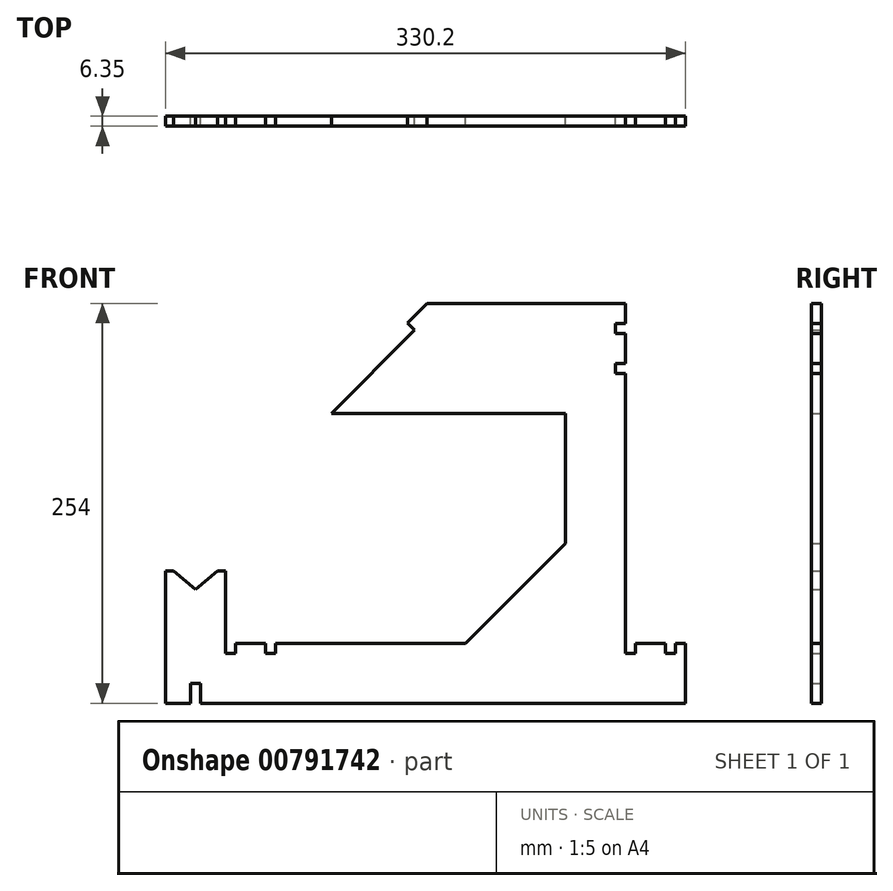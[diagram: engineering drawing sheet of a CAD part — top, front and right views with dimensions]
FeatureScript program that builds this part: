
annotation { "Feature Type Name" : "Feature", "Feature Type Description" : "" }
export const myFeature = defineFeature(function(context is Context, id is Id, definition is map)
    precondition{}
    {
        {
            var Q0;
            Q0=qCreatedBy(makeId("Front.planeOp"),FACE);
            var sketch = newSketch(context, id + "F0", { "sketchPlane" : qUnion([Q0])});
            skLineSegment(sketch, "E0", {"start": v(-82.64, -105.94) * mm, "end": v(-146.14, -169.44) * mm});
            skLineSegment(sketch, "E1", {"start": v(-146.14, -169.44) * mm, "end": v(-266.8, -169.44) * mm});
            skLineSegment(sketch, "E2", {"start": v(-336.64, -207.54) * mm, "end": v(-336.64, -123.4) * mm});
            skCircle(sketch, "E3", {"center": v(-317.6, -118.64) * mm, "radius": 12.7 * mm, "construction": true});
            skLineSegment(sketch, "E4.0", {"start": v(-336.64, -123.4) * mm, "end": v(-331.67, -123.4) * mm});
            skLineSegment(sketch, "E5", {"start": v(-298.54, -123.4) * mm, "end": v(-298.54, -175.79) * mm});
            skLineSegment(sketch, "E6.trimOffspring", {"start": v(-303.5, -123.4) * mm, "end": v(-298.54, -123.4) * mm});
            skPoint(sketch, "E7.orphan", {"position": v(-317.6, -130.6) * mm});
            skLineSegment(sketch, "E8.0", {"start": v(-331.67, -123.4) * mm, "end": v(-317.6, -135.21) * mm});
            skLineSegment(sketch, "E9.0", {"start": v(-303.5, -123.4) * mm, "end": v(-317.6, -135.21) * mm});
            skLineSegment(sketch, "E10", {"start": v(-325.75, -128.36) * mm, "end": v(-317.6, -118.64) * mm, "construction": true});
            skLineSegment(sketch, "E11", {"start": v(-309.43, -128.36) * mm, "end": v(-317.6, -118.64) * mm, "construction": true});
            skLineSegment(sketch, "E12.0", {"start": v(-6.44, -207.54) * mm, "end": v(-314.42, -207.54) * mm});
            skLineSegment(sketch, "E13", {"start": v(-44.54, 46.46) * mm, "end": v(-44.54, 33.76) * mm});
            skLineSegment(sketch, "E14", {"start": v(-38.2, -169.44) * mm, "end": v(-19.14, -169.44) * mm});
            skLineSegment(sketch, "E15", {"start": v(-6.44, -169.44) * mm, "end": v(-6.44, -207.54) * mm});
            skLineSegment(sketch, "E16", {"start": v(-82.64, -105.94) * mm, "end": v(-82.64, -23.39) * mm});
            skLineSegment(sketch, "E17", {"start": v(-231.32, -23.39) * mm, "end": v(-82.64, -23.39) * mm});
            skLineSegment(sketch, "E18.0", {"start": v(-170.45, 46.46) * mm, "end": v(-44.54, 46.46) * mm});
            skLineSegment(sketch, "E19.top", {"start": v(-320.77, -194.84) * mm, "end": v(-314.42, -194.84) * mm});
            skLineSegment(sketch, "E19.left", {"start": v(-320.77, -207.54) * mm, "end": v(-320.77, -194.84) * mm});
            skLineSegment(sketch, "E19.right", {"start": v(-314.42, -207.54) * mm, "end": v(-314.42, -194.84) * mm});
            skLineSegment(sketch, "E20.trimOffspring", {"start": v(-320.77, -207.54) * mm, "end": v(-336.64, -207.54) * mm});
            skLineSegment(sketch, "E21.top", {"start": v(-298.54, -175.79) * mm, "end": v(-292.2, -175.79) * mm});
            skLineSegment(sketch, "E21.right", {"start": v(-292.2, -169.44) * mm, "end": v(-292.2, -175.79) * mm});
            skLineSegment(sketch, "E22.bottom", {"start": v(-273.14, -175.79) * mm, "end": v(-266.8, -175.79) * mm});
            skLineSegment(sketch, "E22.left", {"start": v(-273.14, -175.79) * mm, "end": v(-273.14, -169.44) * mm});
            skLineSegment(sketch, "E22.right", {"start": v(-266.8, -175.79) * mm, "end": v(-266.8, -169.44) * mm});
            skLineSegment(sketch, "E23.trimOffspring", {"start": v(-273.14, -169.44) * mm, "end": v(-292.2, -169.44) * mm});
            skLineSegment(sketch, "E24.top", {"start": v(-44.54, -175.79) * mm, "end": v(-38.2, -175.79) * mm});
            skLineSegment(sketch, "E24.right", {"start": v(-38.2, -169.44) * mm, "end": v(-38.2, -175.79) * mm});
            skLineSegment(sketch, "E25.bottom", {"start": v(-19.14, -175.79) * mm, "end": v(-12.8, -175.79) * mm});
            skLineSegment(sketch, "E25.left", {"start": v(-19.14, -175.79) * mm, "end": v(-19.14, -169.44) * mm});
            skLineSegment(sketch, "E25.right", {"start": v(-12.8, -175.79) * mm, "end": v(-12.8, -169.44) * mm});
            skLineSegment(sketch, "E26.trimOffspring", {"start": v(-12.8, -169.44) * mm, "end": v(-6.44, -169.44) * mm});
            skLineSegment(sketch, "E27.bottom", {"start": v(-44.54, 33.76) * mm, "end": v(-50.9, 33.76) * mm});
            skLineSegment(sketch, "E27.top", {"start": v(-44.54, 27.41) * mm, "end": v(-50.9, 27.41) * mm});
            skLineSegment(sketch, "E27.right", {"start": v(-50.9, 33.76) * mm, "end": v(-50.9, 27.41) * mm});
            skLineSegment(sketch, "E28.bottom", {"start": v(-50.9, 8.36) * mm, "end": v(-44.54, 8.36) * mm});
            skLineSegment(sketch, "E28.top", {"start": v(-50.9, 2.01) * mm, "end": v(-44.54, 2.01) * mm});
            skLineSegment(sketch, "E28.left", {"start": v(-50.9, 8.36) * mm, "end": v(-50.9, 2.01) * mm});
            skLineSegment(sketch, "E29.trimOffspring", {"start": v(-44.54, 27.41) * mm, "end": v(-44.54, 8.36) * mm});
            skLineSegment(sketch, "E30.trimOffspring", {"start": v(-44.54, 2.01) * mm, "end": v(-44.54, -175.79) * mm});
            skLineSegment(sketch, "E31", {"start": v(-317.6, -118.64) * mm, "end": v(-298.07, -99.11) * mm, "construction": true});
            skLineSegment(sketch, "E32.0", {"start": v(-326.57, -109.66) * mm, "end": v(-182.89, 34.03) * mm, "construction": true});
            skLineSegment(sketch, "E33", {"start": v(-182.89, 34.03) * mm, "end": v(-178.4, 29.54) * mm});
            skLineSegment(sketch, "E34", {"start": v(-182.89, 34.03) * mm, "end": v(-170.45, 46.46) * mm});
            skLineSegment(sketch, "E35.trimOffspring", {"start": v(-231.32, -23.39) * mm, "end": v(-178.4, 29.54) * mm});
            skSolve(sketch);
        }
        {
            var Q0;
            Q0=qSketchRegion(id+"F0",true);
            extrude(context, id + "F1", {"entities" : qUnion([Q0]), "depth" : 6.35 * mm, "offsetDistance" : 25.4 * mm});
        }
    });
